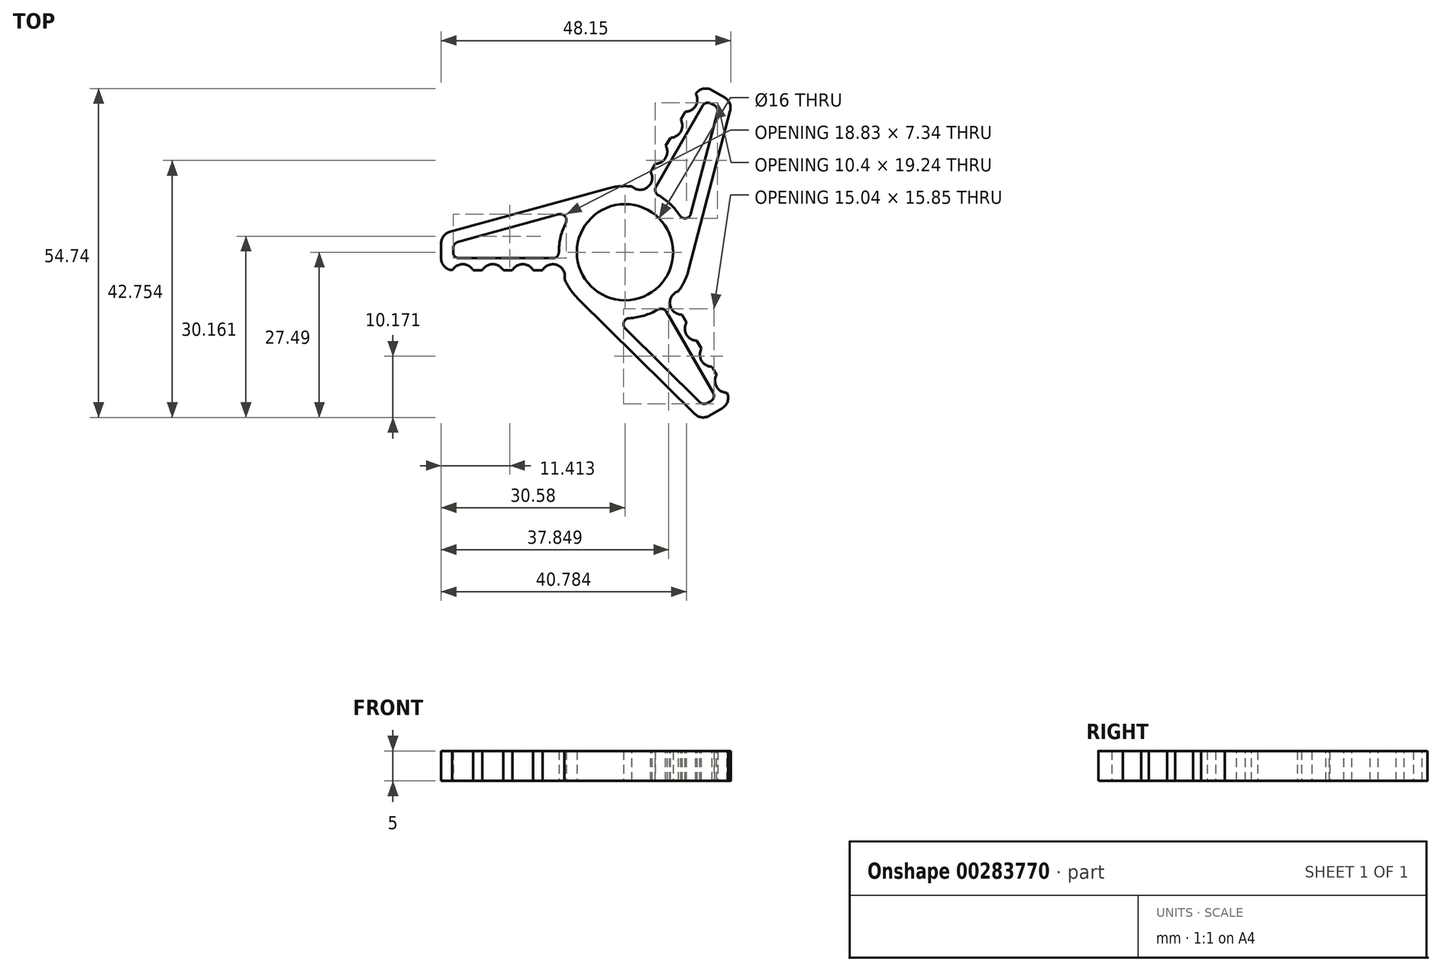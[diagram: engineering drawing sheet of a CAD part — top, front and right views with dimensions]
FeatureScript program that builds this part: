
annotation { "Feature Type Name" : "Feature", "Feature Type Description" : "" }
export const myFeature = defineFeature(function(context is Context, id is Id, definition is map)
    precondition{}
    {
        {
            var Q0;
            Q0=qCreatedBy(makeId("Top.planeOp"),FACE);
            var sketch = newSketch(context, id + "F0", { "sketchPlane" : qUnion([Q0])});
            skCircle(sketch, "E0", {"center": v(0, 0) * mm, "radius": 8 * mm});
            skArc(sketch, "E1", {"start": v(-9.85, 4.9) * mm, "mid": v(-10.7, 2.52) * mm, "end": v(-11, 0) * mm});
            skLineSegment(sketch, "E2", {"start": v(-30, 0) * mm, "end": v(30, 0) * mm, "construction": true});
            skLineSegment(sketch, "E3.0.right", {"start": v(-28.58, -3) * mm, "end": v(-12.33, -3) * mm});
            skLineSegment(sketch, "E4", {"start": v(-29.11, 3.4) * mm, "end": v(-2.92, 10.6) * mm});
            skLineSegment(sketch, "E5", {"start": v(-30.58, 1.48) * mm, "end": v(-30.58, -1) * mm});
            skPoint(sketch, "E6.visualSharp", {"position": v(-30.58, 3) * mm});
            skArc(sketch, "E6.filletArc", {"start": v(-29.11, 3.4) * mm, "mid": v(-30.17, 2.69) * mm, "end": v(-30.58, 1.48) * mm});
            skPoint(sketch, "E7.visualSharp", {"position": v(-30.58, -3) * mm});
            skArc(sketch, "E7.filletArc", {"start": v(-30.58, -1) * mm, "mid": v(-30, -2.41) * mm, "end": v(-28.58, -3) * mm});
            skLineSegment(sketch, "E8.0", {"start": v(-27.85, 1.68) * mm, "end": v(-11.01, 6.3) * mm});
            skLineSegment(sketch, "E8.1", {"start": v(-28.58, 0.71) * mm, "end": v(-28.58, 0) * mm});
            skLineSegment(sketch, "E8.2", {"start": v(-27.58, -1) * mm, "end": v(-12, -1) * mm});
            skArc(sketch, "E9.trimOffspring", {"start": v(-10.05, -4.48) * mm, "mid": v(-9.04, -6.26) * mm, "end": v(-7.73, -7.83) * mm});
            skArc(sketch, "E10.trimOffspring", {"start": v(8.9, -6.46) * mm, "mid": v(9.95, -4.7) * mm, "end": v(10.64, -2.78) * mm});
            skPoint(sketch, "E11.visualSharp", {"position": v(-8.48, 7) * mm});
            skArc(sketch, "E11.filletArc", {"start": v(-9.85, 4.9) * mm, "mid": v(-9.97, 5.98) * mm, "end": v(-11.01, 6.3) * mm});
            skPoint(sketch, "E12.visualSharp", {"position": v(-10.95, -1) * mm});
            skArc(sketch, "E12.filletArc", {"start": v(-12, -1) * mm, "mid": v(-11.3, -0.7) * mm, "end": v(-11, 0) * mm});
            skArc(sketch, "E13.filletArc", {"start": v(-27.85, 1.68) * mm, "mid": v(-28.38, 1.32) * mm, "end": v(-28.58, 0.71) * mm});
            skArc(sketch, "E14.filletArc", {"start": v(-28.58, 0) * mm, "mid": v(-28.3, -0.7) * mm, "end": v(-27.58, -1) * mm});
            skPoint(sketch, "E15.visualSharp", {"position": v(-10.58, -3) * mm});
            skArc(sketch, "E15.filletArc", {"start": v(-10.05, -4.48) * mm, "mid": v(-10.97, -3.4) * mm, "end": v(-12.33, -3) * mm});
            skPoint(sketch, "E16.1.0", {"position": v(6.34, -8.99) * mm});
            skLineSegment(sketch, "E16.1.1", {"start": v(14.66, -23.39) * mm, "end": v(6.87, -9.9) * mm});
            skLineSegment(sketch, "E16.1.2", {"start": v(12.47, -24.96) * mm, "end": v(0.04, -12.69) * mm});
            skPoint(sketch, "E16.1.3", {"position": v(7.89, -7.67) * mm});
            skPoint(sketch, "E16.1.4", {"position": v(17.89, -24.99) * mm});
            skLineSegment(sketch, "E16.1.5", {"start": v(11.6, -26.91) * mm, "end": v(-7.73, -7.83) * mm});
            skLineSegment(sketch, "E16.1.6", {"start": v(16.89, -23.25) * mm, "end": v(8.76, -9.18) * mm});
            skPoint(sketch, "E16.1.7", {"position": v(12.7, -27.99) * mm});
            skArc(sketch, "E16.1.8", {"start": v(0.68, -10.98) * mm, "mid": v(3.18, -10.53) * mm, "end": v(5.5, -9.53) * mm});
            skPoint(sketch, "E16.1.9", {"position": v(-1.82, -10.85) * mm});
            skPoint(sketch, "E16.1.10", {"position": v(13.01, -25.5) * mm});
            skPoint(sketch, "E16.1.11", {"position": v(15.16, -24.25) * mm});
            skArc(sketch, "E16.1.12", {"start": v(16.16, -25.99) * mm, "mid": v(17.09, -24.77) * mm, "end": v(16.89, -23.25) * mm});
            skArc(sketch, "E16.1.13", {"start": v(11.6, -26.91) * mm, "mid": v(12.76, -27.48) * mm, "end": v(14.01, -27.22) * mm});
            skArc(sketch, "E16.1.14", {"start": v(8.9, -6.46) * mm, "mid": v(8.43, -7.8) * mm, "end": v(8.76, -9.18) * mm});
            skArc(sketch, "E16.1.15", {"start": v(0.68, -10.98) * mm, "mid": v(-0.2, -11.63) * mm, "end": v(0.04, -12.69) * mm});
            skLineSegment(sketch, "E16.1.16", {"start": v(14.01, -27.22) * mm, "end": v(16.16, -25.99) * mm});
            skArc(sketch, "E16.1.17", {"start": v(6.87, -9.9) * mm, "mid": v(6.26, -9.43) * mm, "end": v(5.5, -9.53) * mm});
            skArc(sketch, "E16.1.18", {"start": v(14.3, -24.75) * mm, "mid": v(14.76, -24.15) * mm, "end": v(14.66, -23.39) * mm});
            skLineSegment(sketch, "E16.1.19", {"start": v(13.67, -25.11) * mm, "end": v(14.3, -24.75) * mm});
            skArc(sketch, "E16.1.20", {"start": v(12.47, -24.96) * mm, "mid": v(13.05, -25.24) * mm, "end": v(13.67, -25.11) * mm});
            skPoint(sketch, "E16.2.0", {"position": v(4.61, 9.99) * mm});
            skLineSegment(sketch, "E16.2.1", {"start": v(12.93, 24.39) * mm, "end": v(5.13, 10.9) * mm});
            skLineSegment(sketch, "E16.2.2", {"start": v(15.38, 23.28) * mm, "end": v(10.97, 6.38) * mm});
            skPoint(sketch, "E16.2.3", {"position": v(2.7, 10.67) * mm});
            skPoint(sketch, "E16.2.4", {"position": v(12.7, 27.99) * mm});
            skLineSegment(sketch, "E16.2.5", {"start": v(17.5, 23.51) * mm, "end": v(10.64, -2.78) * mm});
            skLineSegment(sketch, "E16.2.6", {"start": v(11.7, 26.25) * mm, "end": v(3.57, 12.18) * mm});
            skPoint(sketch, "E16.2.7", {"position": v(17.89, 24.99) * mm});
            skArc(sketch, "E16.2.8", {"start": v(9.17, 6.08) * mm, "mid": v(7.53, 8.02) * mm, "end": v(5.5, 9.53) * mm});
            skPoint(sketch, "E16.2.9", {"position": v(10.3, 3.85) * mm});
            skPoint(sketch, "E16.2.10", {"position": v(15.57, 24.02) * mm});
            skPoint(sketch, "E16.2.11", {"position": v(13.43, 25.25) * mm});
            skArc(sketch, "E16.2.12", {"start": v(14.43, 26.99) * mm, "mid": v(12.9, 27.19) * mm, "end": v(11.7, 26.25) * mm});
            skArc(sketch, "E16.2.13", {"start": v(17.5, 23.51) * mm, "mid": v(17.41, 24.79) * mm, "end": v(16.57, 25.75) * mm});
            skArc(sketch, "E16.2.14", {"start": v(1.14, 10.94) * mm, "mid": v(2.54, 11.2) * mm, "end": v(3.57, 12.18) * mm});
            skArc(sketch, "E16.2.15", {"start": v(9.17, 6.08) * mm, "mid": v(10.16, 5.65) * mm, "end": v(10.97, 6.38) * mm});
            skLineSegment(sketch, "E16.2.16", {"start": v(16.57, 25.75) * mm, "end": v(14.43, 26.99) * mm});
            skArc(sketch, "E16.2.17", {"start": v(5.13, 10.9) * mm, "mid": v(5.03, 10.13) * mm, "end": v(5.5, 9.53) * mm});
            skArc(sketch, "E16.2.18", {"start": v(14.3, 24.75) * mm, "mid": v(13.53, 24.85) * mm, "end": v(12.93, 24.39) * mm});
            skLineSegment(sketch, "E16.2.19", {"start": v(14.9, 24.4) * mm, "end": v(14.3, 24.75) * mm});
            skArc(sketch, "E16.2.20", {"start": v(15.38, 23.28) * mm, "mid": v(15.33, 23.92) * mm, "end": v(14.9, 24.4) * mm});
            skArc(sketch, "E17.trimOffspring", {"start": v(0.68, -10.98) * mm, "mid": v(1.8, -10.85) * mm, "end": v(2.9, -10.6) * mm});
            skArc(sketch, "E18.trimOffspring", {"start": v(1.14, 10.94) * mm, "mid": v(-0.9, 10.96) * mm, "end": v(-2.92, 10.6) * mm});
            skSolve(sketch);
        }
        {
            var Q0;
            Q0=makeQuery(id+"F0.imprint","IMPRINT",FACE,{"disambiguationData":[TD([[makeQuery(id+"F0.imprint","IMPRINT",EDGE,{"derivedFrom":sQuery(id+"F0.wireOp",EDGE,"E0")}),-1.0]])]});
            extrude(context, id + "F1", {"entities" : qUnion([Q0]), "depth" : 5 * mm, "offsetDistance" : 25 * mm});
        }
        {
            var Q0;
            Q0=makeQuery(id+"F1.opExtrude","CAP_FACE",FACE,{"disambiguationData":[OSD([sQuery(id+"F0.wireOp",EDGE,"E0"),sQuery(id+"F0.wireOp",EDGE,"E1"),sQuery(id+"F0.wireOp",EDGE,"E3.0.left"),sQuery(id+"F0.wireOp",EDGE,"E3.0.right"),sQuery(id+"F0.wireOp",EDGE,"E4"),sQuery(id+"F0.wireOp",EDGE,"WX0Uzkdp-fCQe-VOJW-7FPY-Ezx7dK6Fjs80"),sQuery(id+"F0.wireOp",EDGE,"E5"),sQuery(id+"F0.wireOp",EDGE,"zwgLYqK6-RmX5-3TSH-SCYf-kPdBhvcWHXlf"),sQuery(id+"F0.wireOp",EDGE,"E6.filletArc"),sQuery(id+"F0.wireOp",EDGE,"E7.filletArc"),sQuery(id+"F0.wireOp",EDGE,"d06fb198-a5b9-468b-9813-16c44981fae8.filletArc"),sQuery(id+"F0.wireOp",EDGE,"9e7c56c6-3eec-427f-b9df-32d1be317a37.filletArc"),sQuery(id+"F0.wireOp",EDGE,"32907461-e790-4948-b0b8-d8ebf3a76f47.0"),sQuery(id+"F0.wireOp",EDGE,"32907461-e790-4948-b0b8-d8ebf3a76f47.1"),sQuery(id+"F0.wireOp",EDGE,"32907461-e790-4948-b0b8-d8ebf3a76f47.2"),sQuery(id+"F0.wireOp",EDGE,"E8.0"),sQuery(id+"F0.wireOp",EDGE,"E8.1"),sQuery(id+"F0.wireOp",EDGE,"E8.2"),sQuery(id+"F0.wireOp",EDGE,"E9.trimOffspring"),sQuery(id+"F0.wireOp",EDGE,"E10.trimOffspring"),sQuery(id+"F0.wireOp",EDGE,"f002945e-aa73-4ea2-81e4-c6713d64c543.trimOffspring"),sQuery(id+"F0.wireOp",EDGE,"E11.filletArc"),sQuery(id+"F0.wireOp",EDGE,"E12.filletArc"),sQuery(id+"F0.wireOp",EDGE,"E13.filletArc"),sQuery(id+"F0.wireOp",EDGE,"E14.filletArc"),sQuery(id+"F0.wireOp",EDGE,"125ff90d-cded-4881-bef8-9ce0a9fea3c1.filletArc"),sQuery(id+"F0.wireOp",EDGE,"d565ce6b-4a73-4993-8d7f-3f4f26072821.filletArc"),sQuery(id+"F0.wireOp",EDGE,"4a3642df-f064-4806-9a9b-0e340f525d54.filletArc"),sQuery(id+"F0.wireOp",EDGE,"c47cd775-06dc-4bc7-8bb5-163d83a9279b.filletArc"),sQuery(id+"F0.wireOp",EDGE,"E15.filletArc"),sQuery(id+"F0.wireOp",EDGE,"2a155249-b67a-439b-9d7c-0d743389c6d8.filletArc")])],"isStart":false});
            var sketch = newSketch(context, id + "F2", { "sketchPlane" : qUnion([Q0])});
            skPoint(sketch, "E19.center", {"position": v(0, 0) * mm});
            skCircle(sketch, "E20", {"center": v(-27, -4) * mm, "radius": 2 * mm});
            skCircle(sketch, "E21.1.0.0", {"center": v(-22, -4) * mm, "radius": 2 * mm});
            skCircle(sketch, "E21.2.0.0", {"center": v(-17, -4) * mm, "radius": 2 * mm});
            skCircle(sketch, "E21.3.0.0", {"center": v(-12, -4) * mm, "radius": 2 * mm});
            skLineSegment(sketch, "E21.direction1", {"start": v(-26, -4) * mm, "end": v(-21, -4) * mm, "construction": true});
            skCircle(sketch, "E22.1.0", {"center": v(9.46, -8.4) * mm, "radius": 2 * mm});
            skLineSegment(sketch, "E22.1.1", {"start": v(16.46, -20.52) * mm, "end": v(13.96, -16.19) * mm, "construction": true});
            skCircle(sketch, "E22.1.2", {"center": v(11.96, -12.72) * mm, "radius": 2 * mm});
            skCircle(sketch, "E22.1.3", {"center": v(16.96, -21.38) * mm, "radius": 2 * mm});
            skCircle(sketch, "E22.1.4", {"center": v(14.46, -17.05) * mm, "radius": 2 * mm});
            skCircle(sketch, "E22.2.0", {"center": v(2.54, 12.4) * mm, "radius": 2 * mm});
            skLineSegment(sketch, "E22.2.1", {"start": v(9.54, 24.52) * mm, "end": v(7.04, 20.19) * mm, "construction": true});
            skCircle(sketch, "E22.2.2", {"center": v(5.04, 16.72) * mm, "radius": 2 * mm});
            skCircle(sketch, "E22.2.3", {"center": v(10.04, 25.38) * mm, "radius": 2 * mm});
            skCircle(sketch, "E22.2.4", {"center": v(7.54, 21.05) * mm, "radius": 2 * mm});
            skSolve(sketch);
        }
        {
            var Q0;
            Q0=qSketchRegion(id+"F2",true);
            extrude(context, id + "F3", {"entities" : qUnion([Q0]), "operationType" : NewBodyOperationType.REMOVE, "oppositeDirection" : true, "depth" : 25 * mm, "offsetDistance" : 25 * mm});
        }
    });
